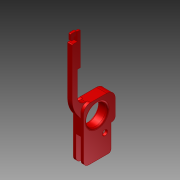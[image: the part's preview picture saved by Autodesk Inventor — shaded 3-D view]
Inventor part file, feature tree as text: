
AUTODESK INVENTOR PART (.ipt)
format: ipt  version: 2012 (Build 160160000, 160)  size: 237,056 bytes
history: native  units: mm
features: fillet x12, extrude x6, sketch x2, chamfer x2
ambient origin geometry x8: Origin, YZ Plane, XZ Plane, XY Plane, X Axis, Y Axis, Z Axis, Center Point
bodies: Solid1 (feature_tree)
feature tree (22):
  sketch  "Sketch2"  dims[d0=6.0mm d4=3.5mm d6=10.0mm]
  extrude  "Extrusion1"  Depth=3.5mm
  fillet  "Fillet1"  Radius=10.0mm
  chamfer  "Chamfer1"  Distance=24.0mm
  chamfer  "Chamfer2"  Distance=17.0mm
  fillet  "Fillet2"  Radius=21.0mm
  extrude  "Extrusion2"  Depth=8.0mm
  fillet  "Fillet5"  Radius=14.0mm
  fillet  "Fillet6"  Radius=5.4mm
  extrude  "Extrusion3"  Depth=2.75mm
  extrude  "Extrusion4"  Depth=66.0mm
  fillet  "Fillet8"  Radius=3.0mm
  fillet  "Fillet9"  Radius=3.0mm
  fillet  "Fillet10"  Radius=5.0mm
  fillet  "Fillet11"  Radius=10.0mm
  fillet  "Fillet12"  Radius=6.2mm
  fillet  "Fillet13"  Radius=12.0mm
  extrude  "Extrusion5"  Depth=39.0mm
  fillet  "Fillet14"  Radius=12.0mm
  fillet  "Fillet15"  Radius=2.0mm
  extrude  "Extrusion7"  Depth=7.0mm
  sketch  "Sketch4"  dims[d7=38.0mm d8=24.0mm d10=17.0mm d11=21.0mm d14=8.0mm d15=14.0mm d16=5.4mm d17=0.0mm d18=2.75mm d19=66.0mm d20=3.0mm d21=6.0mm d22=45.0deg d23=3.0mm d24=6.0mm d25=45.0deg d26=5.0mm d29=10.0mm d30=6.2mm d31=12.0mm d32=39.0mm d33=12.0mm d34=0.0mm d35=2.0mm d36=7.0mm d37=5.0mm d38=6.0mm d39=0.0mm d40=6.0mm d41=0.0mm d43=8.0mm d44=10.0mm d45=62.0mm d46=6.0mm d47=4.0mm d48=30.0mm d49=3.0mm d50=16.5mm d51=26.0mm d52=1.0mm d53=16.0mm d54=3.5mm d55=3.0mm d56=2.5mm d57=2.5mm d58=0.0mm d59=1.25mm d60=1.0mm d61=7.0mm d62=4.0mm d63=4.0mm d66=1.1mm d67=0.0mm]
